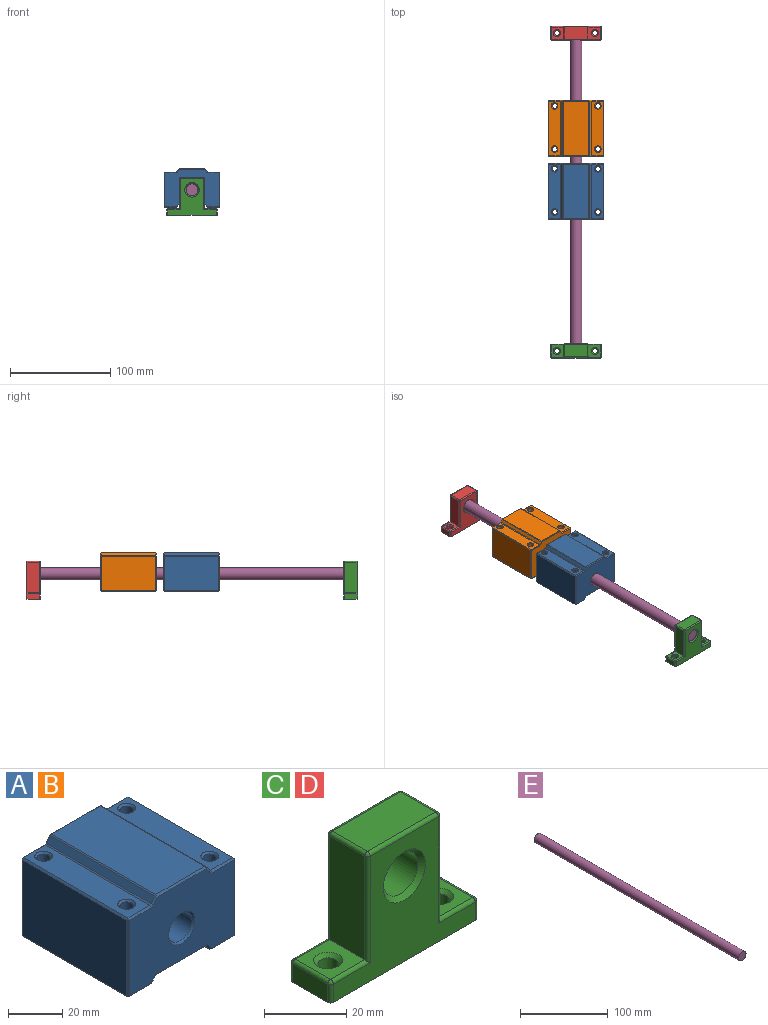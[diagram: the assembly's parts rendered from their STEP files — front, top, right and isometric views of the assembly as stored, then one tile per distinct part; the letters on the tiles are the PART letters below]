
ASSEMBLY  parts=5 mates=4
PART A: 70 faces, bbox 55.9x55.9x38.8 mm
  f0: plane 54.36x12.54mm, normal (0,0,-1), area 642mm2, adj f1,f11,f17,f18,f33,f51
  f1: plane 54.36x34.8mm, normal (1,0,0), area 1891.5mm2, adj f0,f28,f38,f47
  f2: plane 54.36x11.38mm, normal (0,0,1), area 551.4mm2, adj f26,f27,f37,f38,f66,f67
  f3: plane 54.36x2.63mm, normal (0.82,0,0.57), area 174.6mm2, adj f20,f24,f25,f26
  f4: plane 54.36x25.43mm, normal (0,0,1), area 1382.2mm2, adj f23,f24,f35,f36
  f5: plane 54.36x2.63mm, normal (-0.82,0,0.57), area 174.6mm2, adj f34,f35,f45,f46
  f6: plane 54.36x11.38mm, normal (0,0,1), area 551.4mm2, adj f44,f45,f54,f55,f68,f69
  f7: plane 54.36x34.04mm, normal (-1,0,0), area 1850.1mm2, adj f53,f54,f60,f61
  f8: plane 54.36x11.77mm, normal (0,0,-1), area 600.6mm2, adj f9,f15,f16,f52,f60,f64
  f9: plane 54.36x2.81mm, normal (0.78,0,-0.63), area 197.3mm2, adj f8,f10,f48,f62
  f10: plane 54.36x26.22mm, normal (0,0,-1), area 1425.4mm2, adj f9,f11,f43,f59
  f11: plane 54.36x2.81mm, normal (-0.78,0,-0.63), area 197.3mm2, adj f0,f10,f39,f56
  f12: plane 54.36x37.32mm, normal (0,-1,0), area 1711.7mm2, adj f19,f25,f31,f36,f37,f46,f47,f50
  f13: plane 54.36x37.32mm, normal (0,1,0), area 1711.7mm2, adj f20,f22,f23,f27,f28,f33,f34,f39
  f14: cylinder r=6.1mm len=54.36mm, axis (0,1,0), area 2082mm2, adj f19,f65
  f15: cylinder r=2.5mm len=34.8mm, axis (0,0,1), area 547mm2, adj f8,f69
  f16: cylinder r=2.5mm len=34.8mm, axis (0,0,1), area 547mm2, adj f8,f68
  f17: cylinder r=2.5mm len=34.8mm, axis (0,0,1), area 547mm2, adj f0,f66
  f18: cylinder r=2.5mm len=34.8mm, axis (0,0,1), area 547mm2, adj f0,f67
  f19: cone r=6.1mm half-angle=45deg, axis (0,-1,0), area 43.9mm2, adj f12,f14
  f20: plane 3.07x2.46mm, normal (0.58,0.71,0.4), area 3.5mm2, adj f3,f13,f21,f22
  f21: plane 0.76x0.76mm, normal (0.35,0.66,0.66), area 0.4mm2, adj f20,f23,f24
  f22: plane 1.25x1.09mm, normal (0.35,0.66,0.66), area 1.1mm2, adj f13,f20,f26,f27
  f23: plane 25.43x0.76mm, normal (0,0.71,0.71), area 27.4mm2, adj f4,f13,f21,f29
  f24: plane 54.36x0.63mm, normal (0.46,0,0.89), area 38.3mm2, adj f3,f4,f21,f30
  f25: plane 3.07x2.46mm, normal (0.58,-0.71,0.4), area 3.5mm2, adj f3,f12,f30,f31
  f26: plane 54.36x0.63mm, normal (0.46,0,0.89), area 38.3mm2, adj f2,f3,f22,f31
  f27: plane 11.38x0.76mm, normal (0,0.71,0.71), area 12.3mm2, adj f2,f13,f22,f32
  f28: plane 34.8x0.76mm, normal (0.71,0.71,0), area 37.1mm2, adj f1,f13,f32,f33
  f29: plane 0.76x0.76mm, normal (-0.35,0.66,0.66), area 0.4mm2, adj f23,f34,f35
  f30: plane 0.76x0.76mm, normal (0.35,-0.66,0.66), area 0.4mm2, adj f24,f25,f36
  f31: plane 1.25x1.09mm, normal (0.35,-0.66,0.66), area 1.1mm2, adj f12,f25,f26,f37
  f32: plane 0.76x0.76mm, normal (0.58,0.58,0.58), area 0.5mm2, adj f27,f28,f38
  f33: plane 12.54x0.76mm, normal (0,0.71,-0.71), area 12.9mm2, adj f0,f13,f28,f39
  f34: plane 3.07x2.46mm, normal (-0.58,0.71,0.4), area 3.5mm2, adj f5,f13,f29,f40
  f35: plane 54.36x0.63mm, normal (-0.46,0,0.89), area 38.3mm2, adj f4,f5,f29,f41
  f36: plane 25.43x0.76mm, normal (0,-0.71,0.71), area 27.4mm2, adj f4,f12,f30,f41
  f37: plane 11.38x0.76mm, normal (0,-0.71,0.71), area 12.3mm2, adj f2,f12,f31,f42
  f38: plane 54.36x0.76mm, normal (0.71,0,0.71), area 58.6mm2, adj f1,f2,f32,f42
  f39: plane 3.58x2.66mm, normal (-0.55,0.71,-0.45), area 3.9mm2, adj f11,f13,f33,f43
  f40: plane 1.25x1.09mm, normal (-0.35,0.66,0.66), area 1.1mm2, adj f13,f34,f44,f45
  f41: plane 0.76x0.76mm, normal (-0.35,-0.66,0.66), area 0.4mm2, adj f35,f36,f46
  f42: plane 0.76x0.76mm, normal (0.58,-0.58,0.58), area 0.5mm2, adj f37,f38,f47
  f43: plane 26.95x0.76mm, normal (0,0.71,-0.71), area 28.7mm2, adj f10,f13,f39,f48
  f44: plane 11.38x0.76mm, normal (0,0.71,0.71), area 12.3mm2, adj f6,f13,f40,f49
  f45: plane 54.36x0.63mm, normal (-0.46,0,0.89), area 38.3mm2, adj f5,f6,f40,f50
  f46: plane 3.07x2.46mm, normal (-0.58,-0.71,0.4), area 3.5mm2, adj f5,f12,f41,f50
  f47: plane 34.8x0.76mm, normal (0.71,-0.71,0), area 37.1mm2, adj f1,f12,f42,f51
  f48: plane 3.58x2.66mm, normal (0.55,0.71,-0.45), area 3.9mm2, adj f9,f13,f43,f52
  f49: plane 0.76x0.76mm, normal (-0.58,0.58,0.58), area 0.5mm2, adj f44,f53,f54
  f50: plane 1.25x1.09mm, normal (-0.35,-0.66,0.66), area 1.1mm2, adj f12,f45,f46,f55
  f51: plane 12.54x0.76mm, normal (0,-0.71,-0.71), area 12.9mm2, adj f0,f12,f47,f56
  f52: plane 11.77x0.76mm, normal (0,0.71,-0.71), area 12.5mm2, adj f8,f13,f48,f57
  f53: plane 34.04x0.76mm, normal (-0.71,0.71,0), area 36.7mm2, adj f7,f13,f49,f57
  f54: plane 54.36x0.76mm, normal (-0.71,0,0.71), area 58.6mm2, adj f6,f7,f49,f58
  f55: plane 11.38x0.76mm, normal (0,-0.71,0.71), area 12.3mm2, adj f6,f12,f50,f58
  f56: plane 3.58x2.66mm, normal (-0.55,-0.71,-0.45), area 3.9mm2, adj f11,f12,f51,f59
  f57: plane 0.76x0.76mm, normal (-0.58,0.58,-0.58), area 0.5mm2, adj f52,f53,f60
  f58: plane 0.76x0.76mm, normal (-0.58,-0.58,0.58), area 0.5mm2, adj f54,f55,f61
  f59: plane 26.95x0.76mm, normal (0,-0.71,-0.71), area 28.7mm2, adj f10,f12,f56,f62
  f60: plane 54.36x0.76mm, normal (-0.71,0,-0.71), area 58.6mm2, adj f7,f8,f57,f63
  f61: plane 34.04x0.76mm, normal (-0.71,-0.71,0), area 36.7mm2, adj f7,f12,f58,f63
  f62: plane 3.58x2.66mm, normal (0.55,-0.71,-0.45), area 3.9mm2, adj f9,f12,f59,f64
  f63: plane 0.76x0.76mm, normal (-0.58,-0.58,-0.58), area 0.5mm2, adj f60,f61,f64
  f64: plane 11.77x0.76mm, normal (0,-0.71,-0.71), area 12.5mm2, adj f8,f12,f62,f63
  f65: cone r=6.86mm half-angle=45deg, axis (0,1,0), area 43.9mm2, adj f13,f14
  f66: cone r=2.5mm half-angle=45deg, axis (0,0,1), area 19.5mm2, adj f2,f17
  f67: cone r=2.5mm half-angle=45deg, axis (0,0,1), area 19.5mm2, adj f2,f18
  f68: cone r=2.5mm half-angle=45deg, axis (0,0,1), area 19.5mm2, adj f6,f16
  f69: cone r=2.5mm half-angle=45deg, axis (0,0,1), area 19.5mm2, adj f6,f15
PART B: same geometry as A
PART C: 43 faces, bbox 50.8x14x38.1 mm
  f0: plane 12.04x5.39mm, normal (1,0,0), area 64.8mm2, adj f8,f30,f33,f36
  f1: plane 12.04x11.74mm, normal (0,0,1), area 102.4mm2, adj f2,f31,f32,f36,f42
  f2: plane 30.79x12.04mm, normal (1,0,0), area 370.6mm2, adj f1,f24,f28,f29
  f3: plane 23.47x12.04mm, normal (0,0,1), area 282.6mm2, adj f19,f23,f24,f25
  f4: plane 30.79x12.04mm, normal (-1,0,0), area 370.6mm2, adj f5,f18,f19,f20
  f5: plane 12.04x11.74mm, normal (0,0,1), area 102.4mm2, adj f4,f12,f16,f17,f41
  f6: plane 12.04x5.39mm, normal (-1,0,0), area 64.8mm2, adj f8,f11,f12,f13
  f7: cylinder r=5.97mm len=11.94mm, axis (0,1,0), area 428.7mm2, adj f37,f38
  f8: plane 50.8x13.97mm, normal (0,0,-1), area 669.5mm2, adj f0,f6,f9,f10,f11,f13,f30,f33
  f9: plane 48.87x37.14mm, normal (0,-1,0), area 843.7mm2, adj f8,f11,f16,f18,f23,f28,f30,f31
  f10: plane 48.87x37.14mm, normal (0,1,0), area 843.7mm2, adj f8,f13,f17,f20,f25,f29,f32,f33
  f11: cylinder r=0.97mm len=5.39mm, axis (0,0,1), area 8.2mm2, adj f6,f8,f9,f14
  f12: cylinder r=0.97mm len=12.04mm, axis (0,1,0), area 18.3mm2, adj f5,f6,f14,f15
  f13: cylinder r=0.97mm len=5.39mm, axis (0,0,-1), area 8.2mm2, adj f6,f8,f10,f15
  f14: sphere r=0.97mm, area 1.5mm2, adj f11,f12,f16
  f15: sphere r=0.97mm, area 1.5mm2, adj f12,f13,f17
  f16: cylinder r=0.97mm len=12.7mm, axis (1,0,0), area 18.3mm2, adj f5,f9,f14,f18
  f17: cylinder r=0.97mm len=12.7mm, axis (-1,0,0), area 18.3mm2, adj f5,f10,f15,f20
  f18: cylinder r=0.97mm len=31.75mm, axis (0,0,1), area 47.2mm2, adj f4,f9,f16,f21
  f19: cylinder r=0.97mm len=12.04mm, axis (0,-1,0), area 18.3mm2, adj f3,f4,f21,f22
  f20: cylinder r=0.97mm len=31.75mm, axis (0,0,-1), area 47.2mm2, adj f4,f10,f17,f22
  f21: sphere r=0.97mm, area 1.5mm2, adj f18,f19,f23
  f22: sphere r=0.97mm, area 1.5mm2, adj f19,f20,f25
  f23: cylinder r=0.97mm len=23.47mm, axis (1,0,0), area 35.6mm2, adj f3,f9,f21,f26
  f24: cylinder r=0.97mm len=12.04mm, axis (0,1,0), area 18.3mm2, adj f2,f3,f26,f27
  f25: cylinder r=0.97mm len=23.47mm, axis (-1,0,0), area 35.6mm2, adj f3,f10,f22,f27
  f26: sphere r=0.97mm, area 1.5mm2, adj f23,f24,f28
  f27: sphere r=0.97mm, area 1.5mm2, adj f24,f25,f29
  f28: cylinder r=0.97mm len=31.75mm, axis (0,0,-1), area 47.2mm2, adj f2,f9,f26,f31
  f29: cylinder r=0.97mm len=31.75mm, axis (0,0,1), area 47.2mm2, adj f2,f10,f27,f32
  f30: cylinder r=0.97mm len=5.39mm, axis (0,0,-1), area 8.2mm2, adj f0,f8,f9,f34
  f31: cylinder r=0.97mm len=12.7mm, axis (1,0,0), area 18.3mm2, adj f1,f9,f28,f34
  f32: cylinder r=0.97mm len=12.7mm, axis (-1,0,0), area 18.3mm2, adj f1,f10,f29,f35
  f33: cylinder r=0.97mm len=5.39mm, axis (0,0,1), area 8.2mm2, adj f0,f8,f10,f35
  f34: sphere r=0.97mm, area 1.5mm2, adj f30,f31,f36
  f35: sphere r=0.97mm, area 1.5mm2, adj f32,f33,f36
  f36: cylinder r=0.97mm len=12.04mm, axis (0,-1,0), area 18.3mm2, adj f0,f1,f34,f35
  f37: cone r=5.97mm half-angle=45deg, axis (0,-1,0), area 74.5mm2, adj f7,f9
  f38: cone r=7.24mm half-angle=45deg, axis (0,1,0), area 74.5mm2, adj f7,f10
  f39: cylinder r=2.5mm len=5.33mm, axis (0,0,1), area 83.8mm2, adj f8,f42
  f40: cylinder r=2.5mm len=5.33mm, axis (0,0,1), area 83.8mm2, adj f8,f41
  f41: cone r=2.5mm half-angle=45deg, axis (0,0,1), area 27.2mm2, adj f5,f40
  f42: cone r=2.5mm half-angle=45deg, axis (0,0,1), area 27.2mm2, adj f1,f39
PART D: same geometry as C
PART E: 3 faces, bbox 11.9x330.2x11.9 mm
  f0: cylinder r=5.97mm len=330.2mm, axis (0,1,0), area 12383.9mm2, adj f1,f2
  f1: plane 11.94x11.94mm, normal (0,-1,0), area 111.9mm2, adj f0
  f2: plane 11.94x11.94mm, normal (0,1,0), area 111.9mm2, adj f0
PLACE A t=(-201.18,70.36,-1.59)mm
PLACE B t=(-201.18,133.2,-1.59)mm
PLACE C t=(-201.18,-89.03,-23.83)mm
PLACE D t=(-201.18,228.47,-23.83)mm
PLACE E t=(-201.18,70.36,-1.59)mm
MATE fastened D.f7 <-> E.f0  axis (0,1,0) through (-201.18,235.46,-1.59)mm
MATE slider E.f0 <-> B.f14  axis (0,1,0) through (-201.18,70.36,-1.59)mm
MATE fastened C.f7 <-> E.f0  axis (0,1,0) through (-201.18,-94.74,-1.59)mm
MATE slider E.f0 <-> A.f14  axis (0,1,0) through (-201.18,70.36,-1.59)mm
